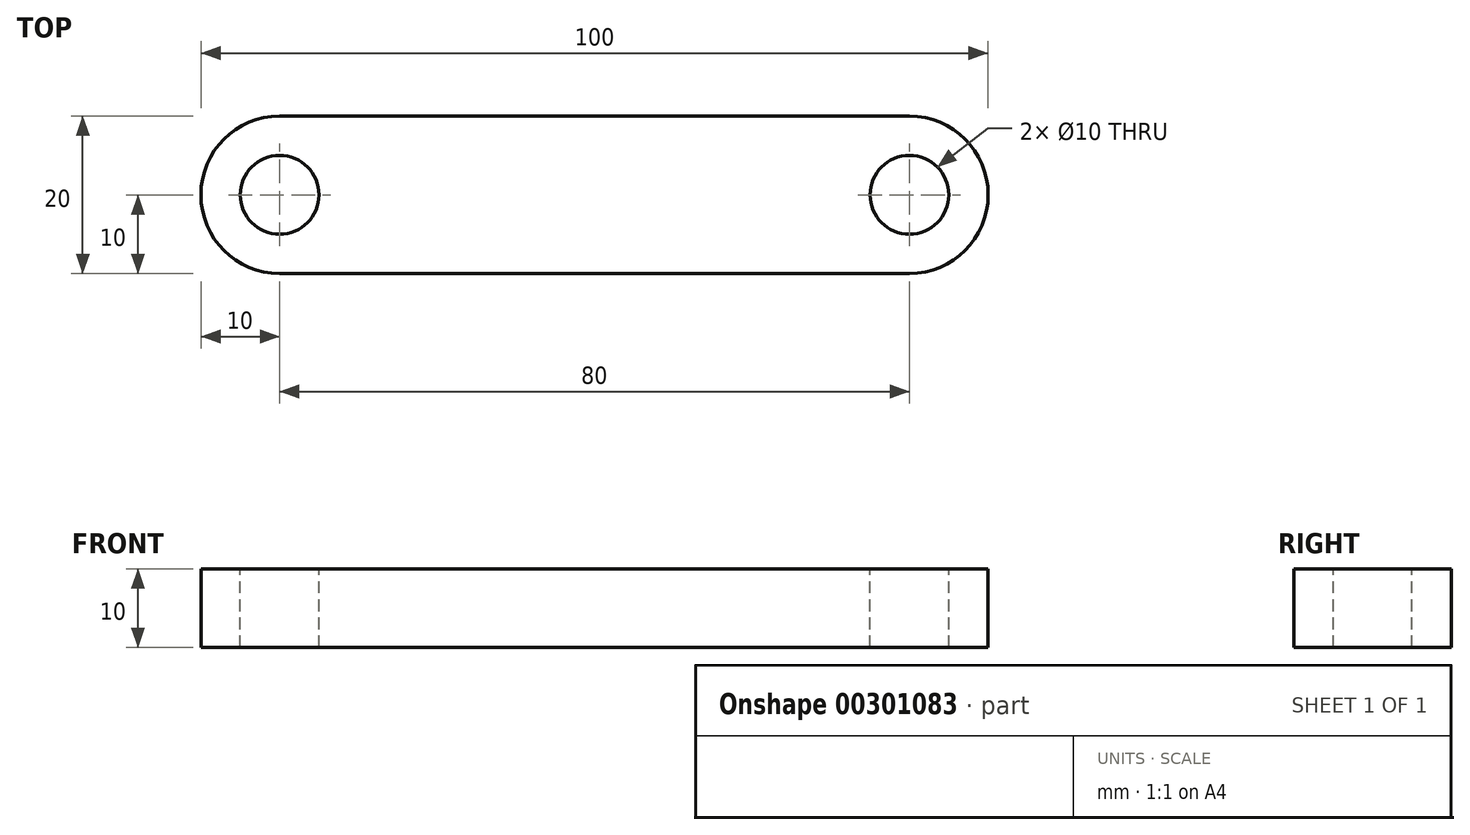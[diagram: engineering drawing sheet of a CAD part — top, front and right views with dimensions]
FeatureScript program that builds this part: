
annotation { "Feature Type Name" : "Feature", "Feature Type Description" : "" }
export const myFeature = defineFeature(function(context is Context, id is Id, definition is map)
    precondition{}
    {
        {
            var Q0;
            Q0=qCreatedBy(makeId("Top.planeOp"),FACE);
            var sketch = newSketch(context, id + "F0", { "sketchPlane" : qUnion([Q0])});
            skLineSegment(sketch, "E0", {"start": v(-80, 10) * mm, "end": v(0, 10) * mm});
            skLineSegment(sketch, "E1", {"start": v(-80, -10) * mm, "end": v(0, -10) * mm});
            skArc(sketch, "E2", {"start": v(0, -10) * mm, "mid": v(10, 0) * mm, "end": v(0, 10) * mm});
            skCircle(sketch, "E3", {"center": v(-80, 0) * mm, "radius": 5 * mm});
            skCircle(sketch, "E4", {"center": v(0, 0) * mm, "radius": 5 * mm});
            skArc(sketch, "E5", {"start": v(-80, 10) * mm, "mid": v(-90, 0) * mm, "end": v(-80, -10) * mm});
            skSolve(sketch);
        }
        {
            var Q0;
            Q0=makeQuery(id+"F0.imprint","IMPRINT",FACE,{"disambiguationData":[TD([[makeQuery(id+"F0.imprint","IMPRINT",EDGE,{"derivedFrom":sQuery(id+"F0.wireOp",EDGE,"E0")}),-1.0]])]});
            extrude(context, id + "F1", {"entities" : qUnion([Q0]), "oppositeDirection" : true, "depth" : 10 * mm});
        }
    });
